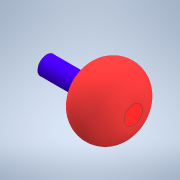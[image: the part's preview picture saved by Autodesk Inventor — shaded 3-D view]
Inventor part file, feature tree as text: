
AUTODESK INVENTOR PART (.ipt)
format: ipt  version: 2021 (Build 250183000, 183)  size: 135,168 bytes
history: native  units: mm
features: revolve x1, sketch x1
ambient origin geometry x8: Origin, YZ Plane, XZ Plane, XY Plane, X Axis, Y Axis, Z Axis, Center Point
bodies: Solid1 (feature_tree)
feature tree (2):
  revolve  "Revolution1"  [1 undecoded]
  sketch  "Sketch1"  dims[d0=2.38mm d1=10.0mm d3=90.0deg]
note: 1 required parameter value undecoded (feature->parameter linkage not recoverable at this tier; creation-order binding heuristic only, values carry confidence <= 0.55)
